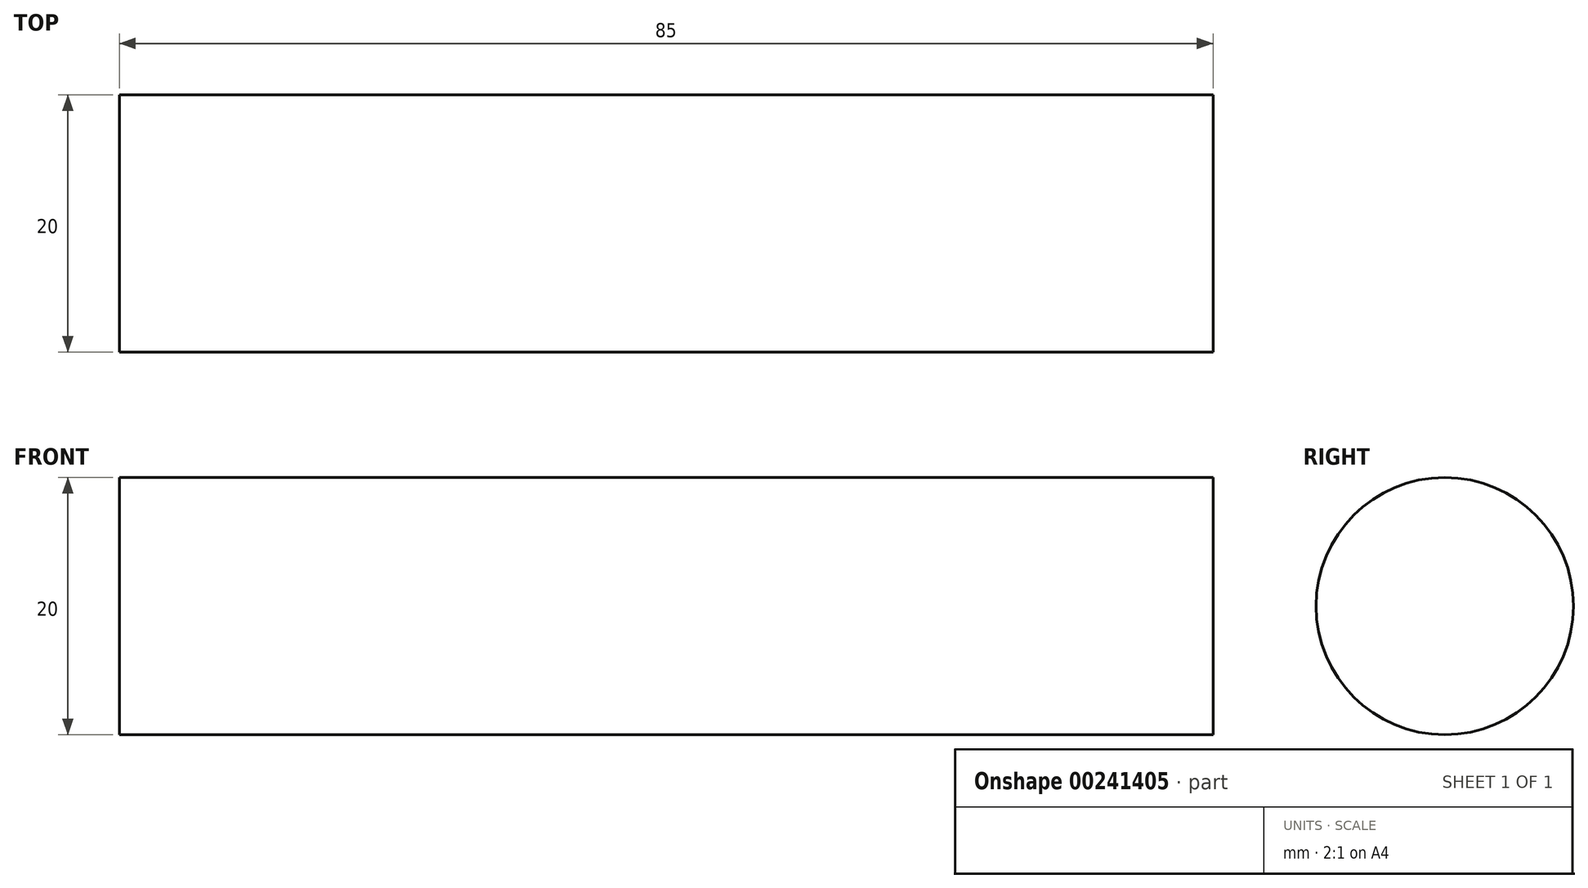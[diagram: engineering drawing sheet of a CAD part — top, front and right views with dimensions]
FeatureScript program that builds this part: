
annotation { "Feature Type Name" : "Feature", "Feature Type Description" : "" }
export const myFeature = defineFeature(function(context is Context, id is Id, definition is map)
    precondition{}
    {
        {
            var Q0;
            Q0=qCreatedBy(makeId("Right.planeOp"),FACE);
            var sketch = newSketch(context, id + "F0", { "sketchPlane" : qUnion([Q0])});
            skCircle(sketch, "E0", {"center": v(0, 0) * mm, "radius": 10 * mm});
            skSolve(sketch);
        }
        {
            var Q0;
            Q0=qSketchRegion(id+"F0",true);
            extrude(context, id + "F1", {"entities" : qUnion([Q0]), "endBound" : BoundingType.SYMMETRIC, "depth" : 85 * mm});
        }
    });
